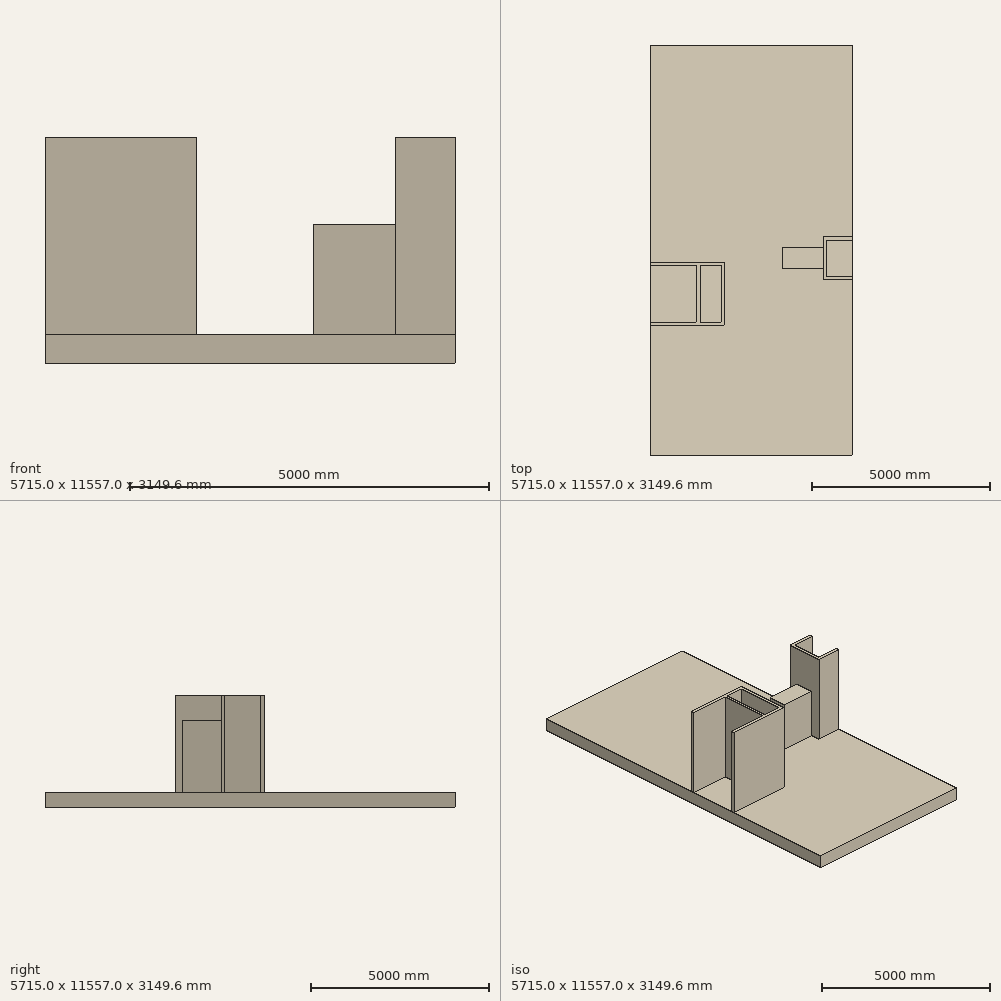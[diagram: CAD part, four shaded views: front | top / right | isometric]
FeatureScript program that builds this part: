
annotation { "Feature Type Name" : "Feature", "Feature Type Description" : "" }
export const myFeature = defineFeature(function(context is Context, id is Id, definition is map)
    precondition{}
    {
        {
            var Q0;
            Q0=qCreatedBy(makeId("Top.planeOp"),FACE);
            var sketch = newSketch(context, id + "F0", { "sketchPlane" : qUnion([Q0])});
            skLineSegment(sketch, "E0.bottom", {"start": v(-2857.5, 5778.5) * mm, "end": v(2857.5, 5778.5) * mm});
            skLineSegment(sketch, "E0.top", {"start": v(-2857.5, -5778.5) * mm, "end": v(2857.5, -5778.5) * mm});
            skLineSegment(sketch, "E0.left", {"start": v(-2857.5, 5778.5) * mm, "end": v(-2857.5, -5778.5) * mm});
            skLineSegment(sketch, "E0.right", {"start": v(2857.5, 5778.5) * mm, "end": v(2857.5, -5778.5) * mm});
            skLineSegment(sketch, "E1.bottom", {"start": v(876.3, -520.7) * mm, "end": v(2019.3, -520.7) * mm});
            skLineSegment(sketch, "E1.top", {"start": v(876.3, 88.9) * mm, "end": v(2019.3, 88.9) * mm});
            skLineSegment(sketch, "E1.left", {"start": v(876.3, -520.7) * mm, "end": v(876.3, 88.9) * mm});
            skLineSegment(sketch, "E1.right", {"start": v(2019.3, -520.7) * mm, "end": v(2019.3, 88.9) * mm});
            skLineSegment(sketch, "E2", {"start": v(2019.3, 88.9) * mm, "end": v(2019.3, 393.7) * mm});
            skLineSegment(sketch, "E3", {"start": v(2019.3, 393.7) * mm, "end": v(2857.5, 393.7) * mm});
            skLineSegment(sketch, "E4", {"start": v(2857.5, 292.1) * mm, "end": v(2120.9, 292.1) * mm});
            skLineSegment(sketch, "E5", {"start": v(2120.9, 292.1) * mm, "end": v(2120.9, -723.9) * mm});
            skLineSegment(sketch, "E6", {"start": v(2120.9, -723.9) * mm, "end": v(2857.5, -723.9) * mm});
            skLineSegment(sketch, "E7", {"start": v(2019.3, -520.7) * mm, "end": v(2019.3, -825.5) * mm});
            skLineSegment(sketch, "E8", {"start": v(2019.3, -825.5) * mm, "end": v(2857.5, -825.5) * mm});
            skLineSegment(sketch, "E9", {"start": v(-2857.5, -2120.9) * mm, "end": v(-749.3, -2120.9) * mm});
            skLineSegment(sketch, "E10", {"start": v(-749.3, -2120.9) * mm, "end": v(-749.3, -330.2) * mm});
            skLineSegment(sketch, "E11", {"start": v(-749.3, -330.2) * mm, "end": v(-2857.5, -330.2) * mm});
            skLineSegment(sketch, "E12", {"start": v(-2857.5, -431.8) * mm, "end": v(-1536.7, -431.8) * mm});
            skLineSegment(sketch, "E13", {"start": v(-1536.7, -431.8) * mm, "end": v(-1536.7, -2019.3) * mm});
            skLineSegment(sketch, "E14", {"start": v(-1536.7, -2019.3) * mm, "end": v(-2857.5, -2019.3) * mm});
            skLineSegment(sketch, "E15.bottom", {"start": v(-1435.1, -431.8) * mm, "end": v(-850.9, -431.8) * mm});
            skLineSegment(sketch, "E15.top", {"start": v(-1435.1, -2019.3) * mm, "end": v(-850.9, -2019.3) * mm});
            skLineSegment(sketch, "E15.left", {"start": v(-1435.1, -431.8) * mm, "end": v(-1435.1, -2019.3) * mm});
            skLineSegment(sketch, "E15.right", {"start": v(-850.9, -431.8) * mm, "end": v(-850.9, -2019.3) * mm});
            skSolve(sketch);
        }
        {
            var Q0;
            {var subQ3=sQuery(id+"F0.wireOp",EDGE,"E9");Q0=makeQuery(id+"F0.imprint","IMPRINT",FACE,{"disambiguationData":[TD([[makeQuery(id+"F0.imprint","IMPRINT",EDGE,{"derivedFrom":subQ3}),1.0]])]});}
            var Q1;
            Q1=makeQuery(id+"F0.imprint","IMPRINT",FACE,{"disambiguationData":[TD([[makeQuery(id+"F0.imprint","IMPRINT",EDGE,{"derivedFrom":sQuery(id+"F0.wireOp",EDGE,"E1.right")}),-1.0]])]});
            extrude(context, id + "F1", {"entities" : qUnion([Q0, Q1]), "depth" : 2743.2 * mm});
        }
        {
            var Q0;
            Q0=makeQuery(id+"F0.imprint","IMPRINT",FACE,{"disambiguationData":[TD([[makeQuery(id+"F0.imprint","IMPRINT",EDGE,{"derivedFrom":sQuery(id+"F0.wireOp",EDGE,"E1.bottom")}),1.0]])]});
            extrude(context, id + "F2", {"entities" : qUnion([Q0]), "depth" : 1524 * mm});
        }
        {
            var Q0;
            Q0 = qSketchRegion(id + "F0", true);
            var Q1;
            Q1=makeQuery(id+"F0.imprint","IMPRINT",FACE,{"disambiguationData":[TD([[makeQuery(id+"F0.imprint","IMPRINT",EDGE,{"derivedFrom":sQuery(id+"F0.wireOp",EDGE,"E15.bottom")}),-1.0]])]});
            var Q2;
            Q2=makeQuery(id+"F0.imprint","IMPRINT",FACE,{"disambiguationData":[TD([[makeQuery(id+"F0.imprint","IMPRINT",EDGE,{"derivedFrom":sQuery(id+"F0.wireOp",EDGE,"E1.bottom")}),1.0]])]});
            extrude(context, id + "F3", {"entities" : qUnion([Q0, Q1, Q2]), "oppositeDirection" : true, "depth" : 406.4 * mm});
        }
        {
            var Q0;
            Q0=makeQuery(id+"F1.opExtrude","SWEPT_FACE",FACE,{"disambiguationData":[OSD([sQuery(id+"F0.wireOp",EDGE,"E10")])]});
            var sketch = newSketch(context, id + "F4", { "sketchPlane" : qUnion([Q0])});
            skLineSegment(sketch, "E16", {"start": v(-1917.7, 0) * mm, "end": v(-1917.7, 2032) * mm});
            skLineSegment(sketch, "E17", {"start": v(-1917.7, 2032) * mm, "end": v(-533.4, 2032) * mm});
            skLineSegment(sketch, "E18", {"start": v(-533.4, 2032) * mm, "end": v(-533.4, 0) * mm});
            skSolve(sketch);
        }
        {
            var Q0;
            {var subQ0=sQuery(id+"F4.wireOp",EDGE,"E16");Q0=makeQuery(id+"F4.imprint","IMPRINT",FACE,{"disambiguationData":[TD([[makeQuery(id+"F4.imprint","IMPRINT",EDGE,{"derivedFrom":subQ0}),-1.0]])]});}
            extrude(context, id + "F5", {"entities" : qUnion([Q0]), "operationType" : NewBodyOperationType.REMOVE, "endBound" : BoundingType.UP_TO_NEXT, "oppositeDirection" : true, "depth" : 25.4 * mm});
        }
    });
